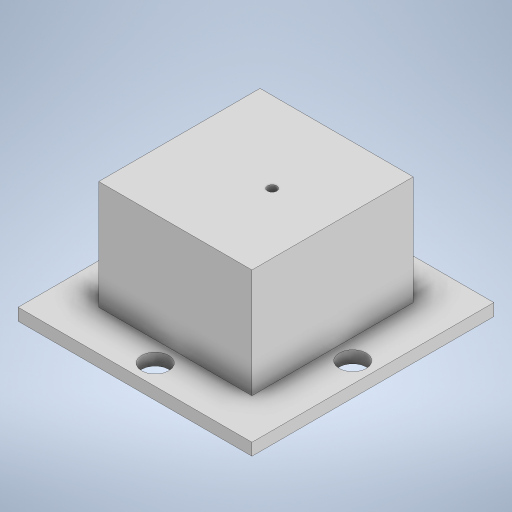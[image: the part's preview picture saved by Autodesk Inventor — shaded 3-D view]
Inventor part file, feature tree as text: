
AUTODESK INVENTOR PART (.ipt)
format: ipt  version: 2024 (Build 280153000, 153)  size: 280,576 bytes
history: native  units: mm
features: extrude x6, sketch x6, plane x3
ambient origin geometry x8: Origin, YZ Plane, XZ Plane, XY Plane, X Axis, Y Axis, Z Axis, Center Point
bodies: Body1 (feature_tree)
feature tree (15):
  plane  "Work Plane5"
  extrude  "Extrusion34"  Depth=40.0mm
  plane  "Work Plane2"
  extrude  "Extrusion35"  Depth=30.0mm
  plane  "Work Plane1"
  extrude  "Extrusion51"  Depth=30.0mm
  sketch  "Sketch77"  dims[d211=10.0mm d212=0.0mm d219=35.0mm]
  extrude  "Extrusion53"  Depth=10.0mm
  extrude  "Extrusion54"  Depth=60.0mm
  extrude  "Extrusion55"  Depth=3.0mm TaperAngle=0.0deg
  sketch  "Sketch45"  dims[d142=38.0mm d143=40.0mm]
  sketch  "Sketch47"  dims[d144=30.0mm d145=0.0mm d146=36.0mm]
  sketch  "Sketch74"  dims[d147=30.0mm d148=-2.617994mm d210=2.3mm]
  sketch  "Sketch78"  dims[d220=58.0mm d221=60.0mm]
  sketch  "Sketch79"  dims[d222=3.0mm d223=0.0mm d224=3.0mm d225=0.0mm d226=6.7mm d227=6.7mm d228=6.7mm d229=0.0mm d230=0.0mm d49=0.5mm d50=0.872665mm d51=0.5mm d52=0.872665mm d130=0.5mm d131=0.872665mm d132=0.5mm d133=0.872665mm d156=0.5mm d157=0.872665mm d158=0.5mm d159=0.872665mm d173=0.5mm d174=0.872665mm d175=0.5mm d176=0.872665mm]
